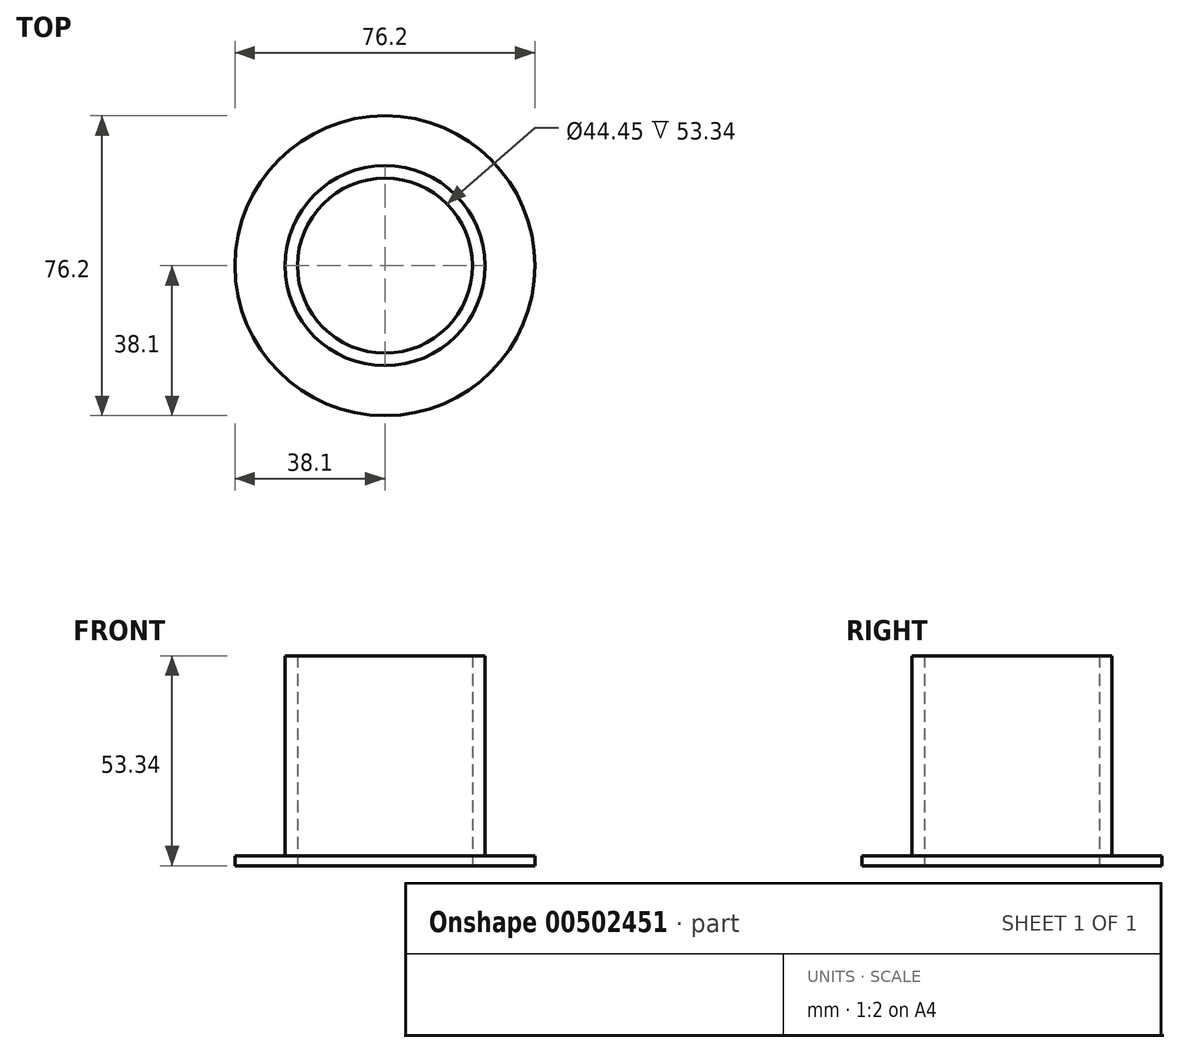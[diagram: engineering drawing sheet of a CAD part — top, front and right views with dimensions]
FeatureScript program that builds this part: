
annotation { "Feature Type Name" : "Feature", "Feature Type Description" : "" }
export const myFeature = defineFeature(function(context is Context, id is Id, definition is map)
    precondition{}
    {
        {
            var Q0;
            Q0=qCreatedBy(makeId("Top.planeOp"),FACE);
            var sketch = newSketch(context, id + "F0", { "sketchPlane" : qUnion([Q0])});
            skCircle(sketch, "E0", {"center": v(0, 0) * mm, "radius": 25.4 * mm});
            skCircle(sketch, "E1", {"center": v(0, 0) * mm, "radius": 22.23 * mm});
            skSolve(sketch);
        }
        {
            var Q0;
            Q0=makeQuery(id+"F0.imprint","IMPRINT",FACE,{"disambiguationData":[TD([[makeQuery(id+"F0.imprint","IMPRINT",EDGE,{"derivedFrom":sQuery(id+"F0.wireOp",EDGE,"E0")}),1.0]])]});
            extrude(context, id + "F1", {"entities" : qUnion([Q0]), "depth" : 50.8 * mm, "offsetDistance" : 25.4 * mm});
        }
        {
            var Q0;
            Q0=qCreatedBy(makeId("Top.planeOp"),FACE);
            var sketch = newSketch(context, id + "F2", { "sketchPlane" : qUnion([Q0])});
            skCircle(sketch, "E2", {"center": v(0, 0) * mm, "radius": 38.1 * mm});
            skCircle(sketch, "E3", {"center": v(0, 0) * mm, "radius": 22.23 * mm});
            skSolve(sketch);
        }
        {
            var Q0;
            Q0=makeQuery(id+"F2.imprint","IMPRINT",FACE,{"disambiguationData":[TD([[makeQuery(id+"F2.imprint","IMPRINT",EDGE,{"derivedFrom":sQuery(id+"F2.wireOp",EDGE,"E2")}),1.0]])]});
            extrude(context, id + "F3", {"entities" : qUnion([Q0]), "operationType" : NewBodyOperationType.ADD, "oppositeDirection" : true, "depth" : 2.54 * mm, "offsetDistance" : 25.4 * mm});
        }
    });
